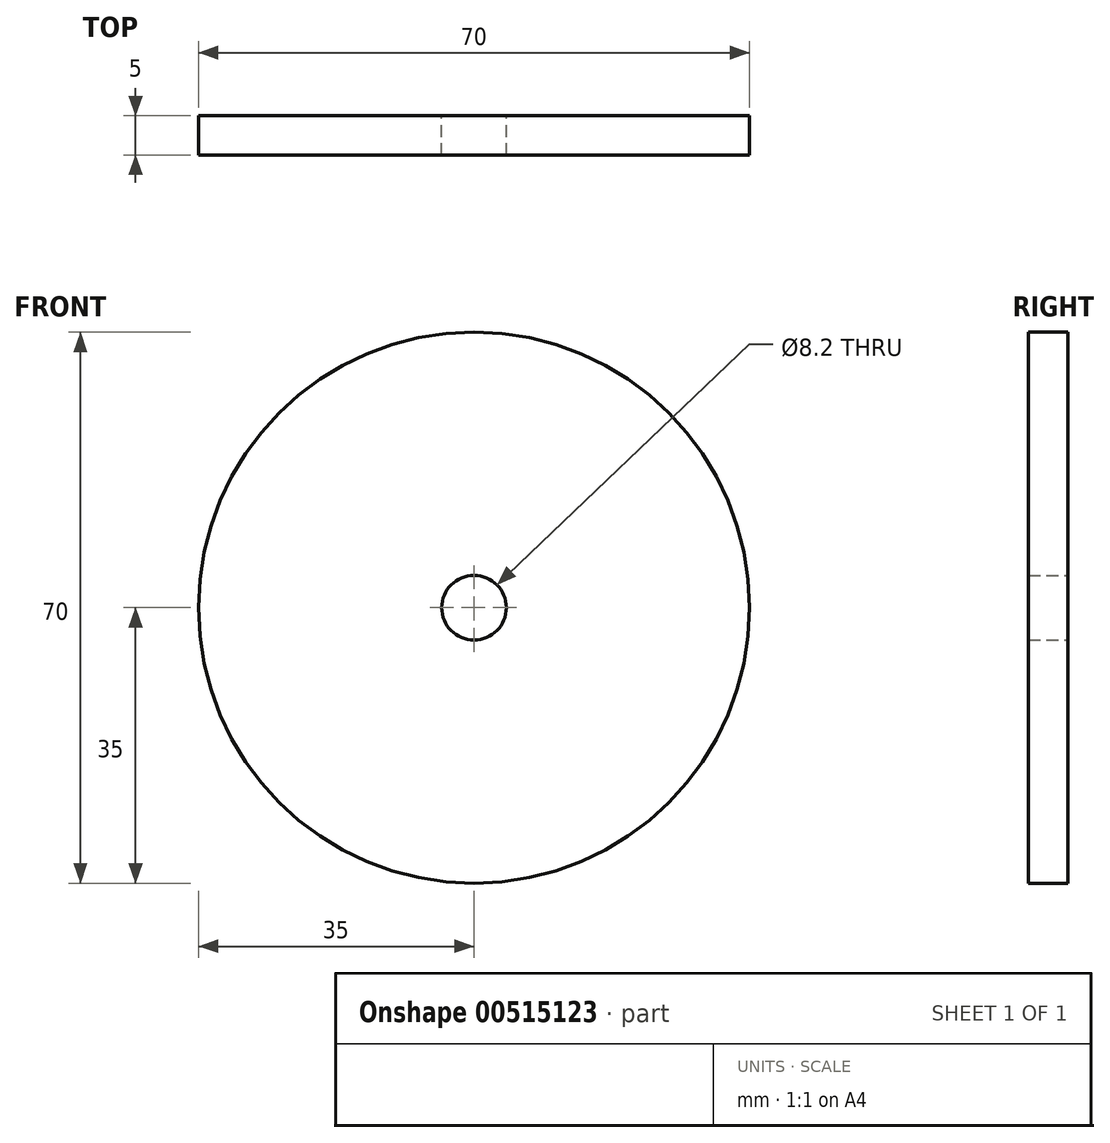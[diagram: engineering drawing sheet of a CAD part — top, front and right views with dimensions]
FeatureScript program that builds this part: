
annotation { "Feature Type Name" : "Feature", "Feature Type Description" : "" }
export const myFeature = defineFeature(function(context is Context, id is Id, definition is map)
    precondition{}
    {
        {
            var Q0;
            Q0=qCreatedBy(makeId("Front.planeOp"),FACE);
            var sketch = newSketch(context, id + "F0", { "sketchPlane" : qUnion([Q0])});
            skCircle(sketch, "E0", {"center": v(0, 0) * mm, "radius": 35 * mm});
            skCircle(sketch, "E1", {"center": v(0, 0) * mm, "radius": 4.1 * mm});
            skSolve(sketch);
        }
        {
            var Q0;
            Q0=makeQuery(id+"F0.imprint","IMPRINT",FACE,{"disambiguationData":[TD([[makeQuery(id+"F0.imprint","IMPRINT",EDGE,{"derivedFrom":sQuery(id+"F0.wireOp",EDGE,"E0")}),1.0]])]});
            extrude(context, id + "F1", {"entities" : qUnion([Q0]), "depth" : 5 * mm, "offsetDistance" : 25 * mm});
        }
    });
